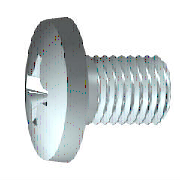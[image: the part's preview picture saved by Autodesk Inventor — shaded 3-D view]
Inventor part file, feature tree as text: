
AUTODESK INVENTOR PART (.ipt)
format: ipt  version: 2014 SP1 (Build 180222100, 222)  size: 267,776 bytes
history: native  units: mm (DEFAULTED — no unit token found)
features: other x2, extrude x1, plane x1
ambient origin geometry x7: Origin, YZ Plane, XZ Plane, X Axis, Y Axis, Z Axis, Center Point
bodies: Solid1 (feature_tree), Body (feature_tree)
feature tree (4):
  other  "IDS_WORKPLANE{1}"
  extrude  "Slot"  Depth=6.35mm
  other  "Cut"
  plane  "Work Plane3"
